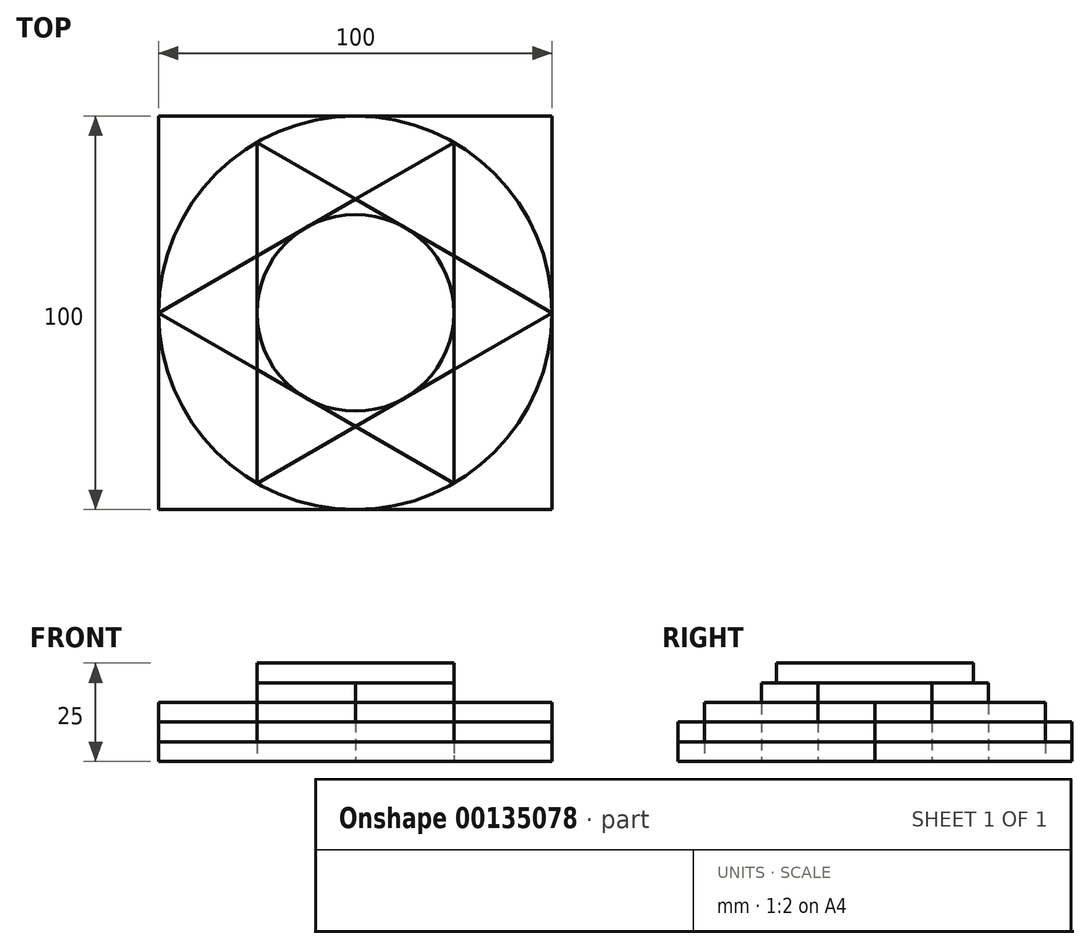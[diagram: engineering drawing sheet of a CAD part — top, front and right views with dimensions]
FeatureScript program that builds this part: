
annotation { "Feature Type Name" : "Feature", "Feature Type Description" : "" }
export const myFeature = defineFeature(function(context is Context, id is Id, definition is map)
    precondition{}
    {
        {
            var Q0;
            Q0=qCreatedBy(makeId("Top.planeOp"),FACE);
            var sketch = newSketch(context, id + "F0", { "sketchPlane" : qUnion([Q0])});
            skCircle(sketch, "E0", {"center": v(0, 0) * mm, "radius": 50 * mm});
            skCircle(sketch, "E1.cCircle", {"center": v(0, 0) * mm, "radius": 50 * mm, "construction": true});
            skLineSegment(sketch, "E1.0", {"start": v(50, 0) * mm, "end": v(25, -43.3) * mm});
            skLineSegment(sketch, "E1.1", {"start": v(25, -43.3) * mm, "end": v(-25, -43.3) * mm});
            skLineSegment(sketch, "E1.2", {"start": v(-25, -43.3) * mm, "end": v(-50, 0) * mm});
            skLineSegment(sketch, "E1.3", {"start": v(-50, 0) * mm, "end": v(-25, 43.3) * mm});
            skLineSegment(sketch, "E1.4", {"start": v(-25, 43.3) * mm, "end": v(25, 43.3) * mm});
            skLineSegment(sketch, "E1.5", {"start": v(25, 43.3) * mm, "end": v(50, 0) * mm});
            skLineSegment(sketch, "E2", {"start": v(25, 43.3) * mm, "end": v(25, -43.3) * mm});
            skLineSegment(sketch, "E3", {"start": v(25, -43.3) * mm, "end": v(-50, 0) * mm});
            skLineSegment(sketch, "E4", {"start": v(-25, 43.3) * mm, "end": v(-25, -43.3) * mm});
            skLineSegment(sketch, "E5", {"start": v(50, 0) * mm, "end": v(-25, 43.3) * mm});
            skLineSegment(sketch, "E6", {"start": v(50, 0) * mm, "end": v(-25, -43.3) * mm});
            skLineSegment(sketch, "E7", {"start": v(25, 43.3) * mm, "end": v(-50, 0) * mm});
            skCircle(sketch, "E8", {"center": v(0, 0) * mm, "radius": 25 * mm});
            skPoint(sketch, "E9.middle", {"position": v(-1.36, 0) * mm});
            skLineSegment(sketch, "E10.0", {"start": v(50, -50) * mm, "end": v(-50, -50) * mm});
            skLineSegment(sketch, "E10.1", {"start": v(-50, -50) * mm, "end": v(-50, 50) * mm});
            skLineSegment(sketch, "E10.2", {"start": v(-50, 50) * mm, "end": v(50, 50) * mm});
            skLineSegment(sketch, "E10.3", {"start": v(50, 50) * mm, "end": v(50, -50) * mm});
            skPoint(sketch, "E10.0.midPoint", {"position": v(0, -50) * mm});
            skSolve(sketch);
        }
        {
            var Q0;
            {var subQ0=sQuery(id+"F0.wireOp",EDGE,"E8");var subQ5=makeQuery(id+"F0.imprint","INTERSECT",VERTEX,{"derivedFrom":[sQuery(id+"F0.wireOp",EDGE,"E2"),subQ0]});Q0=makeQuery(id+"F0.imprint","IMPRINT",FACE,{"disambiguationData":[TD([[makeQuery(id+"F0.imprint","IMPRINT",EDGE,{"disambiguationData":[TD([[subQ5,-1.0]])],"derivedFrom":subQ0}),1.0]])]});}
            extrude(context, id + "F1", {"entities" : qUnion([Q0]), "depth" : 25 * mm});
        }
        {
            var Q0;
            {var subQ0=sQuery(id+"F0.wireOp",EDGE,"E7");var subQ1=sQuery(id+"F0.wireOp",EDGE,"E4");var subQ2=makeQuery(id+"F0.imprint","INTERSECT",VERTEX,{"derivedFrom":[subQ1,subQ0]});Q0=makeQuery(id+"F0.imprint","IMPRINT",FACE,{"disambiguationData":[TD([[makeQuery(id+"F0.imprint","IMPRINT",EDGE,{"disambiguationData":[TD([[subQ2,-1.0]])],"derivedFrom":subQ1}),1.0]])]});}
            var Q1;
            {var subQ0=sQuery(id+"F0.wireOp",EDGE,"E8");var subQ1=sQuery(id+"F0.wireOp",EDGE,"E5");var subQ2=makeQuery(id+"F0.imprint","INTERSECT",VERTEX,{"derivedFrom":[subQ1,subQ0]});Q1=makeQuery(id+"F0.imprint","IMPRINT",FACE,{"disambiguationData":[TD([[makeQuery(id+"F0.imprint","IMPRINT",EDGE,{"disambiguationData":[TD([[subQ2,-1.0]])],"derivedFrom":subQ1}),1.0]])]});}
            var Q2;
            {var subQ0=sQuery(id+"F0.wireOp",EDGE,"E5");var subQ1=sQuery(id+"F0.wireOp",EDGE,"E2");var subQ2=makeQuery(id+"F0.imprint","INTERSECT",VERTEX,{"derivedFrom":[subQ1,subQ0]});Q2=makeQuery(id+"F0.imprint","IMPRINT",FACE,{"disambiguationData":[TD([[makeQuery(id+"F0.imprint","IMPRINT",EDGE,{"disambiguationData":[TD([[subQ2,-1.0]])],"derivedFrom":subQ1}),-1.0]])]});}
            var Q3;
            {var subQ0=sQuery(id+"F0.wireOp",EDGE,"E8");var subQ5=makeQuery(id+"F0.imprint","INTERSECT",VERTEX,{"derivedFrom":[sQuery(id+"F0.wireOp",EDGE,"E2"),subQ0]});Q3=makeQuery(id+"F0.imprint","IMPRINT",FACE,{"disambiguationData":[TD([[makeQuery(id+"F0.imprint","IMPRINT",EDGE,{"disambiguationData":[TD([[subQ5,-1.0]])],"derivedFrom":subQ0}),1.0]])]});}
            var Q4;
            {var subQ0=sQuery(id+"F0.wireOp",EDGE,"E8");var subQ1=sQuery(id+"F0.wireOp",EDGE,"E2");var subQ2=makeQuery(id+"F0.imprint","INTERSECT",VERTEX,{"derivedFrom":[subQ1,subQ0]});Q4=makeQuery(id+"F0.imprint","IMPRINT",FACE,{"disambiguationData":[TD([[makeQuery(id+"F0.imprint","IMPRINT",EDGE,{"disambiguationData":[TD([[subQ2,-1.0]])],"derivedFrom":subQ1}),-1.0]])]});}
            var Q5;
            {var subQ0=sQuery(id+"F0.wireOp",EDGE,"E8");var subQ1=sQuery(id+"F0.wireOp",EDGE,"E2");var subQ2=makeQuery(id+"F0.imprint","INTERSECT",VERTEX,{"derivedFrom":[subQ1,subQ0]});Q5=makeQuery(id+"F0.imprint","IMPRINT",FACE,{"disambiguationData":[TD([[makeQuery(id+"F0.imprint","IMPRINT",EDGE,{"disambiguationData":[TD([[subQ2,-1.0]])],"derivedFrom":subQ1}),-1.0]])]});}
            var Q6;
            {var subQ0=sQuery(id+"F0.wireOp",EDGE,"E6");var subQ1=sQuery(id+"F0.wireOp",EDGE,"E3");var subQ2=makeQuery(id+"F0.imprint","INTERSECT",VERTEX,{"derivedFrom":[subQ1,subQ0]});Q6=makeQuery(id+"F0.imprint","IMPRINT",FACE,{"disambiguationData":[TD([[makeQuery(id+"F0.imprint","IMPRINT",EDGE,{"disambiguationData":[TD([[subQ2,-1.0]])],"derivedFrom":subQ1}),-1.0]])]});}
            var Q7;
            {var subQ0=sQuery(id+"F0.wireOp",EDGE,"E8");var subQ1=sQuery(id+"F0.wireOp",EDGE,"E3");var subQ2=makeQuery(id+"F0.imprint","INTERSECT",VERTEX,{"derivedFrom":[subQ1,subQ0]});Q7=makeQuery(id+"F0.imprint","IMPRINT",FACE,{"disambiguationData":[TD([[makeQuery(id+"F0.imprint","IMPRINT",EDGE,{"disambiguationData":[TD([[subQ2,-1.0]])],"derivedFrom":subQ1}),-1.0]])]});}
            extrude(context, id + "F2", {"entities" : qUnion([Q0, Q1, Q2, Q3, Q4, Q5, Q6, Q7]), "depth" : 20 * mm});
        }
        {
            var Q0;
            {var subQ0=sQuery(id+"F0.wireOp",EDGE,"E7");var subQ3=sQuery(id+"F0.wireOp",EDGE,"E4");var subQ5=makeQuery(id+"F0.imprint","INTERSECT",VERTEX,{"derivedFrom":[subQ3,subQ0]});Q0=makeQuery(id+"F0.imprint","IMPRINT",FACE,{"disambiguationData":[TD([[makeQuery(id+"F0.imprint","IMPRINT",EDGE,{"disambiguationData":[TD([[subQ5,-1.0]])],"derivedFrom":subQ3}),-1.0]])]});}
            var Q1;
            {var subQ0=sQuery(id+"F0.wireOp",EDGE,"E7");var subQ1=sQuery(id+"F0.wireOp",EDGE,"E4");var subQ2=makeQuery(id+"F0.imprint","INTERSECT",VERTEX,{"derivedFrom":[subQ1,subQ0]});Q1=makeQuery(id+"F0.imprint","IMPRINT",FACE,{"disambiguationData":[TD([[makeQuery(id+"F0.imprint","IMPRINT",EDGE,{"disambiguationData":[TD([[subQ2,-1.0]])],"derivedFrom":subQ1}),1.0]])]});}
            var Q2;
            {var subQ0=sQuery(id+"F0.wireOp",EDGE,"E5");var subQ3=sQuery(id+"F0.wireOp",EDGE,"E7");var subQ5=makeQuery(id+"F0.imprint","INTERSECT",VERTEX,{"derivedFrom":[subQ0,subQ3]});Q2=makeQuery(id+"F0.imprint","IMPRINT",FACE,{"disambiguationData":[TD([[makeQuery(id+"F0.imprint","IMPRINT",EDGE,{"disambiguationData":[TD([[subQ5,-1.0]])],"derivedFrom":subQ3}),-1.0]])]});}
            var Q3;
            {var subQ0=sQuery(id+"F0.wireOp",EDGE,"E8");var subQ1=sQuery(id+"F0.wireOp",EDGE,"E5");var subQ2=makeQuery(id+"F0.imprint","INTERSECT",VERTEX,{"derivedFrom":[subQ1,subQ0]});Q3=makeQuery(id+"F0.imprint","IMPRINT",FACE,{"disambiguationData":[TD([[makeQuery(id+"F0.imprint","IMPRINT",EDGE,{"disambiguationData":[TD([[subQ2,-1.0]])],"derivedFrom":subQ1}),1.0]])]});}
            var Q4;
            {var subQ1=sQuery(id+"F0.wireOp",EDGE,"E2");var subQ3=sQuery(id+"F0.wireOp",EDGE,"E5");var subQ4=makeQuery(id+"F0.imprint","INTERSECT",VERTEX,{"derivedFrom":[subQ1,subQ3]});Q4=makeQuery(id+"F0.imprint","IMPRINT",FACE,{"disambiguationData":[TD([[makeQuery(id+"F0.imprint","IMPRINT",EDGE,{"disambiguationData":[TD([[subQ4,-1.0]])],"derivedFrom":subQ3}),-1.0]])]});}
            var Q5;
            {var subQ0=sQuery(id+"F0.wireOp",EDGE,"E5");var subQ1=sQuery(id+"F0.wireOp",EDGE,"E2");var subQ2=makeQuery(id+"F0.imprint","INTERSECT",VERTEX,{"derivedFrom":[subQ1,subQ0]});Q5=makeQuery(id+"F0.imprint","IMPRINT",FACE,{"disambiguationData":[TD([[makeQuery(id+"F0.imprint","IMPRINT",EDGE,{"disambiguationData":[TD([[subQ2,-1.0]])],"derivedFrom":subQ1}),-1.0]])]});}
            var Q6;
            {var subQ0=sQuery(id+"F0.wireOp",EDGE,"E5");var subQ1=sQuery(id+"F0.wireOp",EDGE,"E2");var subQ2=makeQuery(id+"F0.imprint","INTERSECT",VERTEX,{"derivedFrom":[subQ1,subQ0]});Q6=makeQuery(id+"F0.imprint","IMPRINT",FACE,{"disambiguationData":[TD([[makeQuery(id+"F0.imprint","IMPRINT",EDGE,{"disambiguationData":[TD([[subQ2,-1.0]])],"derivedFrom":subQ1}),1.0]])]});}
            var Q7;
            {var subQ0=sQuery(id+"F0.wireOp",EDGE,"E8");var subQ1=sQuery(id+"F0.wireOp",EDGE,"E2");var subQ2=makeQuery(id+"F0.imprint","INTERSECT",VERTEX,{"derivedFrom":[subQ1,subQ0]});Q7=makeQuery(id+"F0.imprint","IMPRINT",FACE,{"disambiguationData":[TD([[makeQuery(id+"F0.imprint","IMPRINT",EDGE,{"disambiguationData":[TD([[subQ2,-1.0]])],"derivedFrom":subQ1}),-1.0]])]});}
            var Q8;
            {var subQ1=sQuery(id+"F0.wireOp",EDGE,"E2");var subQ3=sQuery(id+"F0.wireOp",EDGE,"E6");var subQ4=makeQuery(id+"F0.imprint","INTERSECT",VERTEX,{"derivedFrom":[subQ1,subQ3]});Q8=makeQuery(id+"F0.imprint","IMPRINT",FACE,{"disambiguationData":[TD([[makeQuery(id+"F0.imprint","IMPRINT",EDGE,{"disambiguationData":[TD([[subQ4,-1.0]])],"derivedFrom":subQ3}),1.0]])]});}
            var Q9;
            {var subQ0=sQuery(id+"F0.wireOp",EDGE,"E6");var subQ1=sQuery(id+"F0.wireOp",EDGE,"E3");var subQ2=makeQuery(id+"F0.imprint","INTERSECT",VERTEX,{"derivedFrom":[subQ1,subQ0]});Q9=makeQuery(id+"F0.imprint","IMPRINT",FACE,{"disambiguationData":[TD([[makeQuery(id+"F0.imprint","IMPRINT",EDGE,{"disambiguationData":[TD([[subQ2,-1.0]])],"derivedFrom":subQ1}),-1.0]])]});}
            var Q10;
            {var subQ0=sQuery(id+"F0.wireOp",EDGE,"E6");var subQ1=sQuery(id+"F0.wireOp",EDGE,"E3");var subQ2=makeQuery(id+"F0.imprint","INTERSECT",VERTEX,{"derivedFrom":[subQ1,subQ0]});Q10=makeQuery(id+"F0.imprint","IMPRINT",FACE,{"disambiguationData":[TD([[makeQuery(id+"F0.imprint","IMPRINT",EDGE,{"disambiguationData":[TD([[subQ2,-1.0]])],"derivedFrom":subQ1}),1.0]])]});}
            var Q11;
            {var subQ0=sQuery(id+"F0.wireOp",EDGE,"E8");var subQ1=sQuery(id+"F0.wireOp",EDGE,"E3");var subQ2=makeQuery(id+"F0.imprint","INTERSECT",VERTEX,{"derivedFrom":[subQ1,subQ0]});Q11=makeQuery(id+"F0.imprint","IMPRINT",FACE,{"disambiguationData":[TD([[makeQuery(id+"F0.imprint","IMPRINT",EDGE,{"disambiguationData":[TD([[subQ2,-1.0]])],"derivedFrom":subQ1}),-1.0]])]});}
            var Q12;
            {var subQ0=sQuery(id+"F0.wireOp",EDGE,"E8");var subQ5=makeQuery(id+"F0.imprint","INTERSECT",VERTEX,{"derivedFrom":[sQuery(id+"F0.wireOp",EDGE,"E2"),subQ0]});Q12=makeQuery(id+"F0.imprint","IMPRINT",FACE,{"disambiguationData":[TD([[makeQuery(id+"F0.imprint","IMPRINT",EDGE,{"disambiguationData":[TD([[subQ5,-1.0]])],"derivedFrom":subQ0}),1.0]])]});}
            extrude(context, id + "F3", {"entities" : qUnion([Q0, Q1, Q2, Q3, Q4, Q5, Q6, Q7, Q8, Q9, Q10, Q11, Q12]), "depth" : 15 * mm});
        }
        {
            var Q0;
            {var subQ0=sQuery(id+"F0.wireOp",EDGE,"E1.4");Q0=makeQuery(id+"F0.imprint","IMPRINT",FACE,{"disambiguationData":[TD([[makeQuery(id+"F0.imprint","IMPRINT",EDGE,{"derivedFrom":subQ0}),1.0]])]});}
            var Q1;
            {var subQ0=sQuery(id+"F0.wireOp",EDGE,"E1.5");Q1=makeQuery(id+"F0.imprint","IMPRINT",FACE,{"disambiguationData":[TD([[makeQuery(id+"F0.imprint","IMPRINT",EDGE,{"derivedFrom":subQ0}),1.0]])]});}
            var Q2;
            {var subQ0=sQuery(id+"F0.wireOp",EDGE,"E1.5");Q2=makeQuery(id+"F0.imprint","IMPRINT",FACE,{"disambiguationData":[TD([[makeQuery(id+"F0.imprint","IMPRINT",EDGE,{"derivedFrom":subQ0}),-1.0]])]});}
            var Q3;
            {var subQ1=sQuery(id+"F0.wireOp",EDGE,"E2");var subQ3=sQuery(id+"F0.wireOp",EDGE,"E5");var subQ4=makeQuery(id+"F0.imprint","INTERSECT",VERTEX,{"derivedFrom":[subQ1,subQ3]});Q3=makeQuery(id+"F0.imprint","IMPRINT",FACE,{"disambiguationData":[TD([[makeQuery(id+"F0.imprint","IMPRINT",EDGE,{"disambiguationData":[TD([[subQ4,-1.0]])],"derivedFrom":subQ3}),-1.0]])]});}
            var Q4;
            {var subQ0=sQuery(id+"F0.wireOp",EDGE,"E1.4");Q4=makeQuery(id+"F0.imprint","IMPRINT",FACE,{"disambiguationData":[TD([[makeQuery(id+"F0.imprint","IMPRINT",EDGE,{"derivedFrom":subQ0}),-1.0]])]});}
            var Q5;
            {var subQ0=sQuery(id+"F0.wireOp",EDGE,"E5");var subQ3=sQuery(id+"F0.wireOp",EDGE,"E7");var subQ5=makeQuery(id+"F0.imprint","INTERSECT",VERTEX,{"derivedFrom":[subQ0,subQ3]});Q5=makeQuery(id+"F0.imprint","IMPRINT",FACE,{"disambiguationData":[TD([[makeQuery(id+"F0.imprint","IMPRINT",EDGE,{"disambiguationData":[TD([[subQ5,-1.0]])],"derivedFrom":subQ3}),-1.0]])]});}
            var Q6;
            {var subQ0=sQuery(id+"F0.wireOp",EDGE,"E1.3");Q6=makeQuery(id+"F0.imprint","IMPRINT",FACE,{"disambiguationData":[TD([[makeQuery(id+"F0.imprint","IMPRINT",EDGE,{"derivedFrom":subQ0}),-1.0]])]});}
            var Q7;
            {var subQ0=sQuery(id+"F0.wireOp",EDGE,"E1.3");Q7=makeQuery(id+"F0.imprint","IMPRINT",FACE,{"disambiguationData":[TD([[makeQuery(id+"F0.imprint","IMPRINT",EDGE,{"derivedFrom":subQ0}),1.0]])]});}
            var Q8;
            {var subQ0=sQuery(id+"F0.wireOp",EDGE,"E8");var subQ5=makeQuery(id+"F0.imprint","INTERSECT",VERTEX,{"derivedFrom":[sQuery(id+"F0.wireOp",EDGE,"E2"),subQ0]});Q8=makeQuery(id+"F0.imprint","IMPRINT",FACE,{"disambiguationData":[TD([[makeQuery(id+"F0.imprint","IMPRINT",EDGE,{"disambiguationData":[TD([[subQ5,-1.0]])],"derivedFrom":subQ0}),1.0]])]});}
            var Q9;
            {var subQ0=sQuery(id+"F0.wireOp",EDGE,"E5");var subQ1=sQuery(id+"F0.wireOp",EDGE,"E2");var subQ2=makeQuery(id+"F0.imprint","INTERSECT",VERTEX,{"derivedFrom":[subQ1,subQ0]});Q9=makeQuery(id+"F0.imprint","IMPRINT",FACE,{"disambiguationData":[TD([[makeQuery(id+"F0.imprint","IMPRINT",EDGE,{"disambiguationData":[TD([[subQ2,-1.0]])],"derivedFrom":subQ1}),1.0]])]});}
            var Q10;
            {var subQ0=sQuery(id+"F0.wireOp",EDGE,"E8");var subQ1=sQuery(id+"F0.wireOp",EDGE,"E5");var subQ2=makeQuery(id+"F0.imprint","INTERSECT",VERTEX,{"derivedFrom":[subQ1,subQ0]});Q10=makeQuery(id+"F0.imprint","IMPRINT",FACE,{"disambiguationData":[TD([[makeQuery(id+"F0.imprint","IMPRINT",EDGE,{"disambiguationData":[TD([[subQ2,-1.0]])],"derivedFrom":subQ1}),1.0]])]});}
            var Q11;
            {var subQ0=sQuery(id+"F0.wireOp",EDGE,"E7");var subQ3=sQuery(id+"F0.wireOp",EDGE,"E4");var subQ5=makeQuery(id+"F0.imprint","INTERSECT",VERTEX,{"derivedFrom":[subQ3,subQ0]});Q11=makeQuery(id+"F0.imprint","IMPRINT",FACE,{"disambiguationData":[TD([[makeQuery(id+"F0.imprint","IMPRINT",EDGE,{"disambiguationData":[TD([[subQ5,-1.0]])],"derivedFrom":subQ3}),-1.0]])]});}
            var Q12;
            {var subQ0=sQuery(id+"F0.wireOp",EDGE,"E1.2");Q12=makeQuery(id+"F0.imprint","IMPRINT",FACE,{"disambiguationData":[TD([[makeQuery(id+"F0.imprint","IMPRINT",EDGE,{"derivedFrom":subQ0}),1.0]])]});}
            var Q13;
            {var subQ0=sQuery(id+"F0.wireOp",EDGE,"E6");var subQ1=sQuery(id+"F0.wireOp",EDGE,"E3");var subQ2=makeQuery(id+"F0.imprint","INTERSECT",VERTEX,{"derivedFrom":[subQ1,subQ0]});Q13=makeQuery(id+"F0.imprint","IMPRINT",FACE,{"disambiguationData":[TD([[makeQuery(id+"F0.imprint","IMPRINT",EDGE,{"disambiguationData":[TD([[subQ2,-1.0]])],"derivedFrom":subQ1}),1.0]])]});}
            var Q14;
            {var subQ0=sQuery(id+"F0.wireOp",EDGE,"E1.1");Q14=makeQuery(id+"F0.imprint","IMPRINT",FACE,{"disambiguationData":[TD([[makeQuery(id+"F0.imprint","IMPRINT",EDGE,{"derivedFrom":subQ0}),-1.0]])]});}
            var Q15;
            {var subQ0=sQuery(id+"F0.wireOp",EDGE,"E1.1");Q15=makeQuery(id+"F0.imprint","IMPRINT",FACE,{"disambiguationData":[TD([[makeQuery(id+"F0.imprint","IMPRINT",EDGE,{"derivedFrom":subQ0}),1.0]])]});}
            var Q16;
            {var subQ0=sQuery(id+"F0.wireOp",EDGE,"E1.0");Q16=makeQuery(id+"F0.imprint","IMPRINT",FACE,{"disambiguationData":[TD([[makeQuery(id+"F0.imprint","IMPRINT",EDGE,{"derivedFrom":subQ0}),1.0]])]});}
            var Q17;
            {var subQ0=sQuery(id+"F0.wireOp",EDGE,"E1.0");Q17=makeQuery(id+"F0.imprint","IMPRINT",FACE,{"disambiguationData":[TD([[makeQuery(id+"F0.imprint","IMPRINT",EDGE,{"derivedFrom":subQ0}),-1.0]])]});}
            var Q18;
            {var subQ0=sQuery(id+"F0.wireOp",EDGE,"E8");var subQ1=sQuery(id+"F0.wireOp",EDGE,"E2");var subQ2=makeQuery(id+"F0.imprint","INTERSECT",VERTEX,{"derivedFrom":[subQ1,subQ0]});Q18=makeQuery(id+"F0.imprint","IMPRINT",FACE,{"disambiguationData":[TD([[makeQuery(id+"F0.imprint","IMPRINT",EDGE,{"disambiguationData":[TD([[subQ2,-1.0]])],"derivedFrom":subQ1}),-1.0]])]});}
            var Q19;
            {var subQ1=sQuery(id+"F0.wireOp",EDGE,"E2");var subQ3=sQuery(id+"F0.wireOp",EDGE,"E6");var subQ4=makeQuery(id+"F0.imprint","INTERSECT",VERTEX,{"derivedFrom":[subQ1,subQ3]});Q19=makeQuery(id+"F0.imprint","IMPRINT",FACE,{"disambiguationData":[TD([[makeQuery(id+"F0.imprint","IMPRINT",EDGE,{"disambiguationData":[TD([[subQ4,-1.0]])],"derivedFrom":subQ3}),1.0]])]});}
            var Q20;
            {var subQ0=sQuery(id+"F0.wireOp",EDGE,"E1.2");Q20=makeQuery(id+"F0.imprint","IMPRINT",FACE,{"disambiguationData":[TD([[makeQuery(id+"F0.imprint","IMPRINT",EDGE,{"derivedFrom":subQ0}),-1.0]])]});}
            var Q21;
            {var subQ0=sQuery(id+"F0.wireOp",EDGE,"E8");var subQ1=sQuery(id+"F0.wireOp",EDGE,"E3");var subQ2=makeQuery(id+"F0.imprint","INTERSECT",VERTEX,{"derivedFrom":[subQ1,subQ0]});Q21=makeQuery(id+"F0.imprint","IMPRINT",FACE,{"disambiguationData":[TD([[makeQuery(id+"F0.imprint","IMPRINT",EDGE,{"disambiguationData":[TD([[subQ2,-1.0]])],"derivedFrom":subQ1}),-1.0]])]});}
            var Q22;
            {var subQ0=sQuery(id+"F0.wireOp",EDGE,"E7");var subQ1=sQuery(id+"F0.wireOp",EDGE,"E4");var subQ2=makeQuery(id+"F0.imprint","INTERSECT",VERTEX,{"derivedFrom":[subQ1,subQ0]});Q22=makeQuery(id+"F0.imprint","IMPRINT",FACE,{"disambiguationData":[TD([[makeQuery(id+"F0.imprint","IMPRINT",EDGE,{"disambiguationData":[TD([[subQ2,-1.0]])],"derivedFrom":subQ1}),1.0]])]});}
            var Q23;
            {var subQ0=sQuery(id+"F0.wireOp",EDGE,"E6");var subQ1=sQuery(id+"F0.wireOp",EDGE,"E3");var subQ2=makeQuery(id+"F0.imprint","INTERSECT",VERTEX,{"derivedFrom":[subQ1,subQ0]});Q23=makeQuery(id+"F0.imprint","IMPRINT",FACE,{"disambiguationData":[TD([[makeQuery(id+"F0.imprint","IMPRINT",EDGE,{"disambiguationData":[TD([[subQ2,-1.0]])],"derivedFrom":subQ1}),-1.0]])]});}
            var Q24;
            {var subQ0=sQuery(id+"F0.wireOp",EDGE,"E5");var subQ1=sQuery(id+"F0.wireOp",EDGE,"E2");var subQ2=makeQuery(id+"F0.imprint","INTERSECT",VERTEX,{"derivedFrom":[subQ1,subQ0]});Q24=makeQuery(id+"F0.imprint","IMPRINT",FACE,{"disambiguationData":[TD([[makeQuery(id+"F0.imprint","IMPRINT",EDGE,{"disambiguationData":[TD([[subQ2,-1.0]])],"derivedFrom":subQ1}),-1.0]])]});}
            extrude(context, id + "F4", {"entities" : qUnion([Q0, Q1, Q2, Q3, Q4, Q5, Q6, Q7, Q8, Q9, Q10, Q11, Q12, Q13, Q14, Q15, Q16, Q17, Q18, Q19, Q20, Q21, Q22, Q23, Q24]), "depth" : 10 * mm});
        }
        {
            var Q0;
            {var subQ3=sQuery(id+"F0.wireOp",EDGE,"E10.2");var subQ5=sQuery(id+"F0.wireOp",EDGE,"E10.1");var subQ7=makeQuery(id+"F0.imprint","INTERSECT",VERTEX,{"derivedFrom":[subQ5,subQ3]});Q0=makeQuery(id+"F0.imprint","IMPRINT",FACE,{"disambiguationData":[TD([[makeQuery(id+"F0.imprint","IMPRINT",EDGE,{"disambiguationData":[TD([[subQ7,-1.0]])],"derivedFrom":subQ3}),-1.0]])]});}
            var Q1;
            {var subQ0=sQuery(id+"F0.wireOp",EDGE,"E10.3");var subQ5=sQuery(id+"F0.wireOp",EDGE,"E10.2");var subQ7=makeQuery(id+"F0.imprint","INTERSECT",VERTEX,{"derivedFrom":[subQ5,subQ0]});Q1=makeQuery(id+"F0.imprint","IMPRINT",FACE,{"disambiguationData":[TD([[makeQuery(id+"F0.imprint","IMPRINT",EDGE,{"disambiguationData":[TD([[subQ7,1.0]])],"derivedFrom":subQ5}),-1.0]])]});}
            var Q2;
            {var subQ0=sQuery(id+"F0.wireOp",EDGE,"E1.4");Q2=makeQuery(id+"F0.imprint","IMPRINT",FACE,{"disambiguationData":[TD([[makeQuery(id+"F0.imprint","IMPRINT",EDGE,{"derivedFrom":subQ0}),1.0]])]});}
            var Q3;
            {var subQ0=sQuery(id+"F0.wireOp",EDGE,"E1.4");Q3=makeQuery(id+"F0.imprint","IMPRINT",FACE,{"disambiguationData":[TD([[makeQuery(id+"F0.imprint","IMPRINT",EDGE,{"derivedFrom":subQ0}),-1.0]])]});}
            var Q4;
            {var subQ1=sQuery(id+"F0.wireOp",EDGE,"E2");var subQ3=sQuery(id+"F0.wireOp",EDGE,"E5");var subQ4=makeQuery(id+"F0.imprint","INTERSECT",VERTEX,{"derivedFrom":[subQ1,subQ3]});Q4=makeQuery(id+"F0.imprint","IMPRINT",FACE,{"disambiguationData":[TD([[makeQuery(id+"F0.imprint","IMPRINT",EDGE,{"disambiguationData":[TD([[subQ4,-1.0]])],"derivedFrom":subQ3}),-1.0]])]});}
            var Q5;
            {var subQ0=sQuery(id+"F0.wireOp",EDGE,"E1.5");Q5=makeQuery(id+"F0.imprint","IMPRINT",FACE,{"disambiguationData":[TD([[makeQuery(id+"F0.imprint","IMPRINT",EDGE,{"derivedFrom":subQ0}),-1.0]])]});}
            var Q6;
            {var subQ0=sQuery(id+"F0.wireOp",EDGE,"E1.5");Q6=makeQuery(id+"F0.imprint","IMPRINT",FACE,{"disambiguationData":[TD([[makeQuery(id+"F0.imprint","IMPRINT",EDGE,{"derivedFrom":subQ0}),1.0]])]});}
            var Q7;
            {var subQ0=sQuery(id+"F0.wireOp",EDGE,"E5");var subQ3=sQuery(id+"F0.wireOp",EDGE,"E7");var subQ5=makeQuery(id+"F0.imprint","INTERSECT",VERTEX,{"derivedFrom":[subQ0,subQ3]});Q7=makeQuery(id+"F0.imprint","IMPRINT",FACE,{"disambiguationData":[TD([[makeQuery(id+"F0.imprint","IMPRINT",EDGE,{"disambiguationData":[TD([[subQ5,-1.0]])],"derivedFrom":subQ3}),-1.0]])]});}
            var Q8;
            {var subQ0=sQuery(id+"F0.wireOp",EDGE,"E1.3");Q8=makeQuery(id+"F0.imprint","IMPRINT",FACE,{"disambiguationData":[TD([[makeQuery(id+"F0.imprint","IMPRINT",EDGE,{"derivedFrom":subQ0}),-1.0]])]});}
            var Q9;
            {var subQ0=sQuery(id+"F0.wireOp",EDGE,"E1.3");Q9=makeQuery(id+"F0.imprint","IMPRINT",FACE,{"disambiguationData":[TD([[makeQuery(id+"F0.imprint","IMPRINT",EDGE,{"derivedFrom":subQ0}),1.0]])]});}
            var Q10;
            {var subQ0=sQuery(id+"F0.wireOp",EDGE,"E7");var subQ3=sQuery(id+"F0.wireOp",EDGE,"E4");var subQ5=makeQuery(id+"F0.imprint","INTERSECT",VERTEX,{"derivedFrom":[subQ3,subQ0]});Q10=makeQuery(id+"F0.imprint","IMPRINT",FACE,{"disambiguationData":[TD([[makeQuery(id+"F0.imprint","IMPRINT",EDGE,{"disambiguationData":[TD([[subQ5,-1.0]])],"derivedFrom":subQ3}),-1.0]])]});}
            var Q11;
            {var subQ0=sQuery(id+"F0.wireOp",EDGE,"E5");var subQ1=sQuery(id+"F0.wireOp",EDGE,"E2");var subQ2=makeQuery(id+"F0.imprint","INTERSECT",VERTEX,{"derivedFrom":[subQ1,subQ0]});Q11=makeQuery(id+"F0.imprint","IMPRINT",FACE,{"disambiguationData":[TD([[makeQuery(id+"F0.imprint","IMPRINT",EDGE,{"disambiguationData":[TD([[subQ2,-1.0]])],"derivedFrom":subQ1}),1.0]])]});}
            var Q12;
            {var subQ0=sQuery(id+"F0.wireOp",EDGE,"E1.0");Q12=makeQuery(id+"F0.imprint","IMPRINT",FACE,{"disambiguationData":[TD([[makeQuery(id+"F0.imprint","IMPRINT",EDGE,{"derivedFrom":subQ0}),1.0]])]});}
            var Q13;
            {var subQ0=sQuery(id+"F0.wireOp",EDGE,"E1.0");Q13=makeQuery(id+"F0.imprint","IMPRINT",FACE,{"disambiguationData":[TD([[makeQuery(id+"F0.imprint","IMPRINT",EDGE,{"derivedFrom":subQ0}),-1.0]])]});}
            var Q14;
            {var subQ1=sQuery(id+"F0.wireOp",EDGE,"E2");var subQ3=sQuery(id+"F0.wireOp",EDGE,"E6");var subQ4=makeQuery(id+"F0.imprint","INTERSECT",VERTEX,{"derivedFrom":[subQ1,subQ3]});Q14=makeQuery(id+"F0.imprint","IMPRINT",FACE,{"disambiguationData":[TD([[makeQuery(id+"F0.imprint","IMPRINT",EDGE,{"disambiguationData":[TD([[subQ4,-1.0]])],"derivedFrom":subQ3}),1.0]])]});}
            var Q15;
            {var subQ0=sQuery(id+"F0.wireOp",EDGE,"E8");var subQ1=sQuery(id+"F0.wireOp",EDGE,"E2");var subQ2=makeQuery(id+"F0.imprint","INTERSECT",VERTEX,{"derivedFrom":[subQ1,subQ0]});Q15=makeQuery(id+"F0.imprint","IMPRINT",FACE,{"disambiguationData":[TD([[makeQuery(id+"F0.imprint","IMPRINT",EDGE,{"disambiguationData":[TD([[subQ2,-1.0]])],"derivedFrom":subQ1}),-1.0]])]});}
            var Q16;
            {var subQ0=sQuery(id+"F0.wireOp",EDGE,"E8");var subQ1=sQuery(id+"F0.wireOp",EDGE,"E3");var subQ2=makeQuery(id+"F0.imprint","INTERSECT",VERTEX,{"derivedFrom":[subQ1,subQ0]});Q16=makeQuery(id+"F0.imprint","IMPRINT",FACE,{"disambiguationData":[TD([[makeQuery(id+"F0.imprint","IMPRINT",EDGE,{"disambiguationData":[TD([[subQ2,-1.0]])],"derivedFrom":subQ1}),-1.0]])]});}
            var Q17;
            {var subQ0=sQuery(id+"F0.wireOp",EDGE,"E6");var subQ1=sQuery(id+"F0.wireOp",EDGE,"E3");var subQ2=makeQuery(id+"F0.imprint","INTERSECT",VERTEX,{"derivedFrom":[subQ1,subQ0]});Q17=makeQuery(id+"F0.imprint","IMPRINT",FACE,{"disambiguationData":[TD([[makeQuery(id+"F0.imprint","IMPRINT",EDGE,{"disambiguationData":[TD([[subQ2,-1.0]])],"derivedFrom":subQ1}),1.0]])]});}
            var Q18;
            {var subQ0=sQuery(id+"F0.wireOp",EDGE,"E1.1");Q18=makeQuery(id+"F0.imprint","IMPRINT",FACE,{"disambiguationData":[TD([[makeQuery(id+"F0.imprint","IMPRINT",EDGE,{"derivedFrom":subQ0}),-1.0]])]});}
            var Q19;
            {var subQ0=sQuery(id+"F0.wireOp",EDGE,"E1.2");Q19=makeQuery(id+"F0.imprint","IMPRINT",FACE,{"disambiguationData":[TD([[makeQuery(id+"F0.imprint","IMPRINT",EDGE,{"derivedFrom":subQ0}),1.0]])]});}
            var Q20;
            {var subQ0=sQuery(id+"F0.wireOp",EDGE,"E1.2");Q20=makeQuery(id+"F0.imprint","IMPRINT",FACE,{"disambiguationData":[TD([[makeQuery(id+"F0.imprint","IMPRINT",EDGE,{"derivedFrom":subQ0}),-1.0]])]});}
            var Q21;
            {var subQ3=sQuery(id+"F0.wireOp",EDGE,"E10.1");var subQ5=sQuery(id+"F0.wireOp",EDGE,"E10.0");var subQ7=makeQuery(id+"F0.imprint","INTERSECT",VERTEX,{"derivedFrom":[subQ5,subQ3]});Q21=makeQuery(id+"F0.imprint","IMPRINT",FACE,{"disambiguationData":[TD([[makeQuery(id+"F0.imprint","IMPRINT",EDGE,{"disambiguationData":[TD([[subQ7,1.0]])],"derivedFrom":subQ5}),-1.0]])]});}
            var Q22;
            {var subQ3=sQuery(id+"F0.wireOp",EDGE,"E10.0");var subQ5=sQuery(id+"F0.wireOp",EDGE,"E10.3");var subQ7=makeQuery(id+"F0.imprint","INTERSECT",VERTEX,{"derivedFrom":[subQ3,subQ5]});Q22=makeQuery(id+"F0.imprint","IMPRINT",FACE,{"disambiguationData":[TD([[makeQuery(id+"F0.imprint","IMPRINT",EDGE,{"disambiguationData":[TD([[subQ7,-1.0]])],"derivedFrom":subQ3}),-1.0]])]});}
            var Q23;
            {var subQ0=sQuery(id+"F0.wireOp",EDGE,"E1.1");Q23=makeQuery(id+"F0.imprint","IMPRINT",FACE,{"disambiguationData":[TD([[makeQuery(id+"F0.imprint","IMPRINT",EDGE,{"derivedFrom":subQ0}),1.0]])]});}
            var Q24;
            {var subQ0=sQuery(id+"F0.wireOp",EDGE,"E7");var subQ1=sQuery(id+"F0.wireOp",EDGE,"E4");var subQ2=makeQuery(id+"F0.imprint","INTERSECT",VERTEX,{"derivedFrom":[subQ1,subQ0]});Q24=makeQuery(id+"F0.imprint","IMPRINT",FACE,{"disambiguationData":[TD([[makeQuery(id+"F0.imprint","IMPRINT",EDGE,{"disambiguationData":[TD([[subQ2,-1.0]])],"derivedFrom":subQ1}),1.0]])]});}
            var Q25;
            {var subQ0=sQuery(id+"F0.wireOp",EDGE,"E8");var subQ1=sQuery(id+"F0.wireOp",EDGE,"E5");var subQ2=makeQuery(id+"F0.imprint","INTERSECT",VERTEX,{"derivedFrom":[subQ1,subQ0]});Q25=makeQuery(id+"F0.imprint","IMPRINT",FACE,{"disambiguationData":[TD([[makeQuery(id+"F0.imprint","IMPRINT",EDGE,{"disambiguationData":[TD([[subQ2,-1.0]])],"derivedFrom":subQ1}),1.0]])]});}
            var Q26;
            {var subQ0=sQuery(id+"F0.wireOp",EDGE,"E5");var subQ1=sQuery(id+"F0.wireOp",EDGE,"E2");var subQ2=makeQuery(id+"F0.imprint","INTERSECT",VERTEX,{"derivedFrom":[subQ1,subQ0]});Q26=makeQuery(id+"F0.imprint","IMPRINT",FACE,{"disambiguationData":[TD([[makeQuery(id+"F0.imprint","IMPRINT",EDGE,{"disambiguationData":[TD([[subQ2,-1.0]])],"derivedFrom":subQ1}),-1.0]])]});}
            var Q27;
            {var subQ0=sQuery(id+"F0.wireOp",EDGE,"E8");var subQ5=makeQuery(id+"F0.imprint","INTERSECT",VERTEX,{"derivedFrom":[sQuery(id+"F0.wireOp",EDGE,"E2"),subQ0]});Q27=makeQuery(id+"F0.imprint","IMPRINT",FACE,{"disambiguationData":[TD([[makeQuery(id+"F0.imprint","IMPRINT",EDGE,{"disambiguationData":[TD([[subQ5,-1.0]])],"derivedFrom":subQ0}),1.0]])]});}
            var Q28;
            {var subQ0=sQuery(id+"F0.wireOp",EDGE,"E6");var subQ1=sQuery(id+"F0.wireOp",EDGE,"E3");var subQ2=makeQuery(id+"F0.imprint","INTERSECT",VERTEX,{"derivedFrom":[subQ1,subQ0]});Q28=makeQuery(id+"F0.imprint","IMPRINT",FACE,{"disambiguationData":[TD([[makeQuery(id+"F0.imprint","IMPRINT",EDGE,{"disambiguationData":[TD([[subQ2,-1.0]])],"derivedFrom":subQ1}),-1.0]])]});}
            extrude(context, id + "F5", {"entities" : qUnion([Q0, Q1, Q2, Q3, Q4, Q5, Q6, Q7, Q8, Q9, Q10, Q11, Q12, Q13, Q14, Q15, Q16, Q17, Q18, Q19, Q20, Q21, Q22, Q23, Q24, Q25, Q26, Q27, Q28]), "depth" : 5 * mm});
        }
    });
